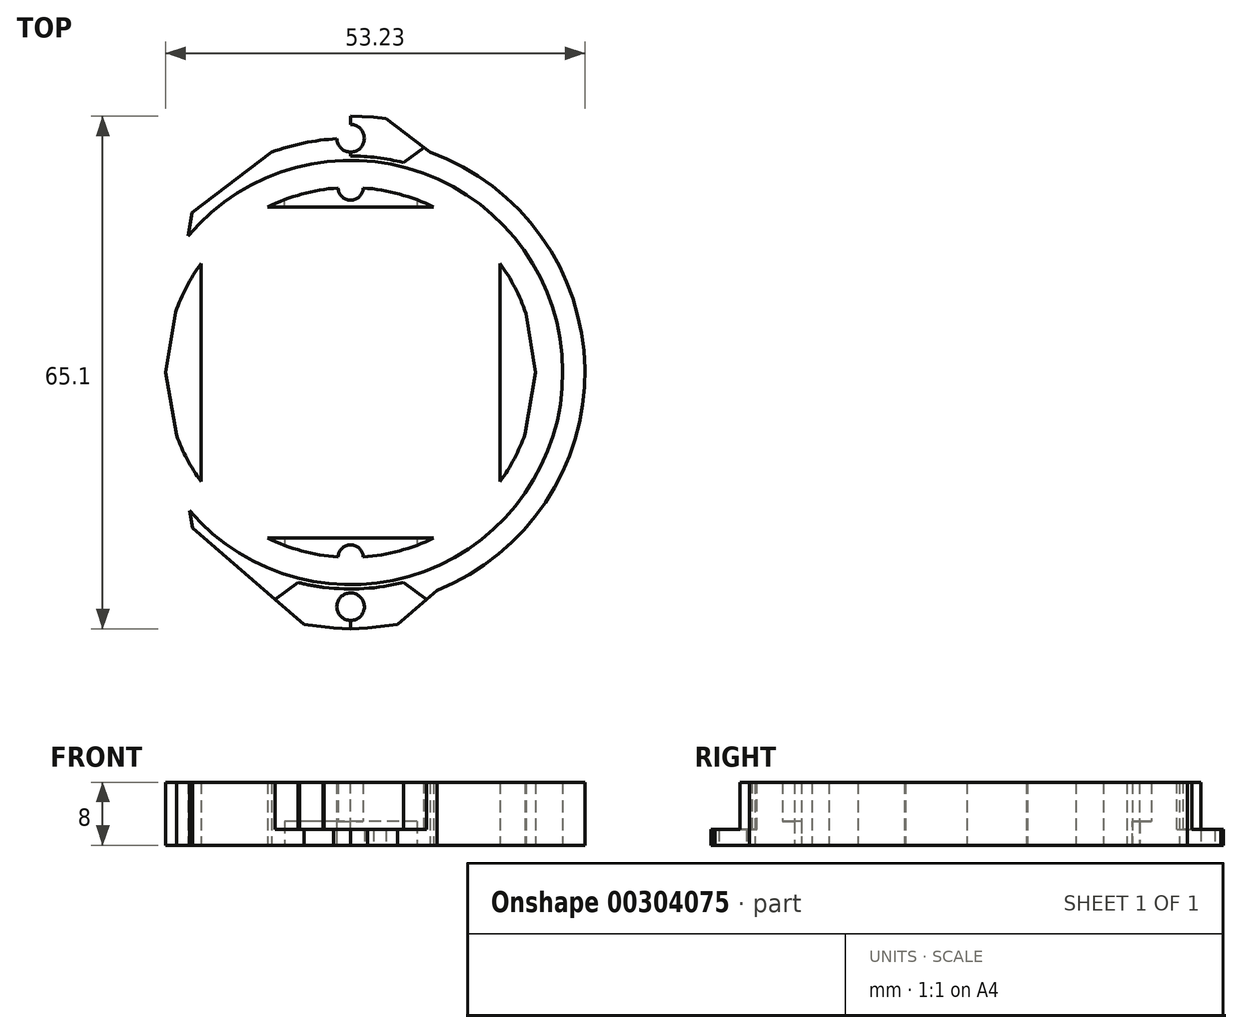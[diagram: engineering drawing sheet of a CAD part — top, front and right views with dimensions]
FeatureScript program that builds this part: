
annotation { "Feature Type Name" : "Feature", "Feature Type Description" : "" }
export const myFeature = defineFeature(function(context is Context, id is Id, definition is map)
    precondition{}
    {
        {
            var Q0;
            Q0=qCreatedBy(makeId("Top.planeOp"),FACE);
            var sketch = newSketch(context, id + "F0", { "sketchPlane" : qUnion([Q0])});
            skCircle(sketch, "E0", {"center": v(0, 0) * mm, "radius": 29.75 * mm});
            skCircle(sketch, "E1.0", {"center": v(0, 0) * mm, "radius": 32.55 * mm});
            skCircle(sketch, "E2.0", {"center": v(0, 0) * mm, "radius": 26.95 * mm});
            skCircle(sketch, "E3", {"center": v(0, 29.75) * mm, "radius": 1.75 * mm});
            skCircle(sketch, "E4", {"center": v(0, -29.75) * mm, "radius": 1.75 * mm});
            skPoint(sketch, "E5.visualSharp", {"position": v(18.58, -23.24) * mm});
            skCircle(sketch, "E6", {"center": v(0, 0) * mm, "radius": 23.5 * mm});
            skCircle(sketch, "E7", {"center": v(0, -23.5) * mm, "radius": 1.6 * mm});
            skCircle(sketch, "E8", {"center": v(0, 23.5) * mm, "radius": 1.6 * mm});
            skLineSegment(sketch, "E9", {"start": v(0, -32.55) * mm, "end": v(2.18, -32.48) * mm});
            skLineSegment(sketch, "E10", {"start": v(2.18, -32.48) * mm, "end": v(5.95, -32) * mm});
            skLineSegment(sketch, "E11", {"start": v(5.95, -32) * mm, "end": v(20.12, -19.72) * mm});
            skLineSegment(sketch, "E12", {"start": v(20.12, -19.72) * mm, "end": v(23.5, 0) * mm});
            skLineSegment(sketch, "E13", {"start": v(23.5, 0) * mm, "end": v(20.16, 20.34) * mm});
            skLineSegment(sketch, "E14", {"start": v(20.16, 20.34) * mm, "end": v(4.5, 32.24) * mm});
            skLineSegment(sketch, "E15", {"start": v(4.5, 32.24) * mm, "end": v(2.88, 32.42) * mm});
            skLineSegment(sketch, "E16", {"start": v(2.88, 32.42) * mm, "end": v(0.01, 32.55) * mm});
            skLineSegment(sketch, "E17", {"start": v(0.01, 32.55) * mm, "end": v(0.01, 18.5) * mm});
            skLineSegment(sketch, "E18", {"start": v(0, -18.5) * mm, "end": v(0, -32.55) * mm});
            skLineSegment(sketch, "E19.MirrorCS", {"start": v(-2.86, 32.42) * mm, "end": v(0.01, 32.55) * mm});
            skLineSegment(sketch, "E20.MirrorCS", {"start": v(-4.47, 32.24) * mm, "end": v(-2.86, 32.42) * mm});
            skLineSegment(sketch, "E21.MirrorCS", {"start": v(-20.13, 20.34) * mm, "end": v(-4.47, 32.24) * mm});
            skLineSegment(sketch, "E22.MirrorCS", {"start": v(-23.48, 0) * mm, "end": v(-20.13, 20.34) * mm});
            skLineSegment(sketch, "E23.MirrorCS", {"start": v(-20.1, -19.72) * mm, "end": v(-23.48, 0) * mm});
            skLineSegment(sketch, "E24.MirrorCS", {"start": v(-5.92, -32) * mm, "end": v(-20.1, -19.72) * mm});
            skLineSegment(sketch, "E25.MirrorCS", {"start": v(-2.16, -32.48) * mm, "end": v(-5.92, -32) * mm});
            skLineSegment(sketch, "E26.MirrorCS", {"start": v(0.02, -32.55) * mm, "end": v(-2.16, -32.48) * mm});
            skLineSegment(sketch, "E27.MirrorCS", {"start": v(0.02, -18.5) * mm, "end": v(0.02, -32.55) * mm});
            skSolve(sketch);
        }
        {
            var Q0;
            {var subQ0=sQuery(id+"F0.wireOp",EDGE,"E19.MirrorCS");Q0=makeQuery(id+"F0.imprint","IMPRINT",FACE,{"disambiguationData":[TD([[makeQuery(id+"F0.imprint","IMPRINT",EDGE,{"derivedFrom":subQ0}),-1.0]])]});}
            var Q1;
            {var subQ0=sQuery(id+"F0.wireOp",EDGE,"E15");Q1=makeQuery(id+"F0.imprint","IMPRINT",FACE,{"disambiguationData":[TD([[makeQuery(id+"F0.imprint","IMPRINT",EDGE,{"derivedFrom":subQ0}),1.0]])]});}
            var Q2;
            {var subQ5=sQuery(id+"F0.wireOp",EDGE,"E3");var subQ6=sQuery(id+"F0.wireOp",EDGE,"E0");var subQ7=makeQuery(id+"F0.imprint","INTERSECT",VERTEX,{"disambiguationData":[OD(0.0)],"derivedFrom":[subQ6,subQ5]});Q2=makeQuery(id+"F0.imprint","IMPRINT",FACE,{"disambiguationData":[TD([[makeQuery(id+"F0.imprint","IMPRINT",EDGE,{"disambiguationData":[TD([[subQ7,1.0]])],"derivedFrom":subQ6}),1.0]])]});}
            var Q3;
            {var subQ1=sQuery(id+"F0.wireOp",EDGE,"E3");var subQ9=sQuery(id+"F0.wireOp",EDGE,"E0");var subQ10=makeQuery(id+"F0.imprint","INTERSECT",VERTEX,{"disambiguationData":[OD(1.0)],"derivedFrom":[subQ9,subQ1]});Q3=makeQuery(id+"F0.imprint","IMPRINT",FACE,{"disambiguationData":[TD([[makeQuery(id+"F0.imprint","IMPRINT",EDGE,{"disambiguationData":[TD([[subQ10,-1.0]])],"derivedFrom":subQ9}),1.0]])]});}
            var Q4;
            {var subQ0=sQuery(id+"F0.wireOp",EDGE,"E17");var subQ1=sQuery(id+"F0.wireOp",EDGE,"E2.0");var subQ2=makeQuery(id+"F0.imprint","INTERSECT",VERTEX,{"derivedFrom":[subQ1,subQ0]});Q4=makeQuery(id+"F0.imprint","IMPRINT",FACE,{"disambiguationData":[TD([[makeQuery(id+"F0.imprint","IMPRINT",EDGE,{"disambiguationData":[TD([[subQ2,1.0]])],"derivedFrom":subQ1}),-1.0]])]});}
            var Q5;
            {var subQ1=sQuery(id+"F0.wireOp",EDGE,"E2.0");var subQ7=sQuery(id+"F0.wireOp",EDGE,"E17");var subQ9=makeQuery(id+"F0.imprint","INTERSECT",VERTEX,{"derivedFrom":[subQ1,subQ7]});Q5=makeQuery(id+"F0.imprint","IMPRINT",FACE,{"disambiguationData":[TD([[makeQuery(id+"F0.imprint","IMPRINT",EDGE,{"disambiguationData":[TD([[subQ9,-1.0]])],"derivedFrom":subQ1}),-1.0]])]});}
            var Q6;
            {var subQ2=sQuery(id+"F0.wireOp",EDGE,"E6");var subQ4=sQuery(id+"F0.wireOp",EDGE,"E13");var subQ14=makeQuery(id+"F0.imprint","INTERSECT",VERTEX,{"derivedFrom":[subQ2,subQ4]});Q6=makeQuery(id+"F0.imprint","IMPRINT",FACE,{"disambiguationData":[TD([[makeQuery(id+"F0.imprint","IMPRINT",EDGE,{"disambiguationData":[TD([[subQ14,-1.0]])],"derivedFrom":subQ2}),1.0]])]});}
            var Q7;
            {var subQ0=sQuery(id+"F0.wireOp",EDGE,"E18");var subQ1=sQuery(id+"F0.wireOp",EDGE,"E2.0");var subQ2=makeQuery(id+"F0.imprint","INTERSECT",VERTEX,{"derivedFrom":[subQ1,subQ0]});Q7=makeQuery(id+"F0.imprint","IMPRINT",FACE,{"disambiguationData":[TD([[makeQuery(id+"F0.imprint","IMPRINT",EDGE,{"disambiguationData":[TD([[subQ2,-1.0]])],"derivedFrom":subQ1}),-1.0]])]});}
            var Q8;
            {var subQ7=sQuery(id+"F0.wireOp",EDGE,"E24.MirrorCS");var subQ9=sQuery(id+"F0.wireOp",EDGE,"E0");var subQ10=makeQuery(id+"F0.imprint","INTERSECT",VERTEX,{"derivedFrom":[subQ9,subQ7]});Q8=makeQuery(id+"F0.imprint","IMPRINT",FACE,{"disambiguationData":[TD([[makeQuery(id+"F0.imprint","IMPRINT",EDGE,{"disambiguationData":[TD([[subQ10,-1.0]])],"derivedFrom":subQ9}),1.0]])]});}
            var Q9;
            {var subQ0=sQuery(id+"F0.wireOp",EDGE,"E25.MirrorCS");Q9=makeQuery(id+"F0.imprint","IMPRINT",FACE,{"disambiguationData":[TD([[makeQuery(id+"F0.imprint","IMPRINT",EDGE,{"derivedFrom":subQ0}),-1.0]])]});}
            var Q10;
            {var subQ0=sQuery(id+"F0.wireOp",EDGE,"E10");Q10=makeQuery(id+"F0.imprint","IMPRINT",FACE,{"disambiguationData":[TD([[makeQuery(id+"F0.imprint","IMPRINT",EDGE,{"derivedFrom":subQ0}),1.0]])]});}
            var Q11;
            {var subQ7=sQuery(id+"F0.wireOp",EDGE,"E0");var subQ9=sQuery(id+"F0.wireOp",EDGE,"E4");var subQ10=makeQuery(id+"F0.imprint","INTERSECT",VERTEX,{"disambiguationData":[OD(1.0)],"derivedFrom":[subQ7,subQ9]});Q11=makeQuery(id+"F0.imprint","IMPRINT",FACE,{"disambiguationData":[TD([[makeQuery(id+"F0.imprint","IMPRINT",EDGE,{"disambiguationData":[TD([[subQ10,-1.0]])],"derivedFrom":subQ7}),1.0]])]});}
            var Q12;
            {var subQ0=sQuery(id+"F0.wireOp",EDGE,"E12");var subQ1=sQuery(id+"F0.wireOp",EDGE,"E2.0");var subQ2=makeQuery(id+"F0.imprint","INTERSECT",VERTEX,{"derivedFrom":[subQ1,subQ0]});Q12=makeQuery(id+"F0.imprint","IMPRINT",FACE,{"disambiguationData":[TD([[makeQuery(id+"F0.imprint","IMPRINT",EDGE,{"disambiguationData":[TD([[subQ2,-1.0]])],"derivedFrom":subQ1}),-1.0]])]});}
            extrude(context, id + "F1", {"entities" : qUnion([Q0, Q1, Q2, Q3, Q4, Q5, Q6, Q7, Q8, Q9, Q10, Q11, Q12]), "depth" : 8 * mm});
        }
        {
            var Q0;
            Q0=makeQuery(id+"F1.opExtrude","CAP_FACE",FACE,{"disambiguationData":[OSD([sQuery(id+"F0.wireOp",EDGE,"E3"),sQuery(id+"F0.wireOp",EDGE,"E4"),sQuery(id+"F0.wireOp",EDGE,"E7"),sQuery(id+"F0.wireOp",EDGE,"E8"),sQuery(id+"F0.wireOp",EDGE,"5pVUo4Kb-ogc3-tZgz-UWGt-Z78I515m52U4.bottom"),sQuery(id+"F0.wireOp",EDGE,"5pVUo4Kb-ogc3-tZgz-UWGt-Z78I515m52U4.top"),sQuery(id+"F0.wireOp",EDGE,"5pVUo4Kb-ogc3-tZgz-UWGt-Z78I515m52U4.left"),sQuery(id+"F0.wireOp",EDGE,"5pVUo4Kb-ogc3-tZgz-UWGt-Z78I515m52U4.right"),sQuery(id+"F0.wireOp",EDGE,"E9"),sQuery(id+"F0.wireOp",EDGE,"E10"),sQuery(id+"F0.wireOp",EDGE,"E11"),sQuery(id+"F0.wireOp",EDGE,"E12"),sQuery(id+"F0.wireOp",EDGE,"E13"),sQuery(id+"F0.wireOp",EDGE,"E14"),sQuery(id+"F0.wireOp",EDGE,"E15"),sQuery(id+"F0.wireOp",EDGE,"E16"),sQuery(id+"F0.wireOp",EDGE,"2KKQg4aQ-yS0h-yKgR-9ZTe-73FSqlJjfBOo"),sQuery(id+"F0.wireOp",EDGE,"E18"),sQuery(id+"F0.wireOp",EDGE,"E19.MirrorCS"),sQuery(id+"F0.wireOp",EDGE,"E20.MirrorCS"),sQuery(id+"F0.wireOp",EDGE,"E21.MirrorCS"),sQuery(id+"F0.wireOp",EDGE,"E22.MirrorCS"),sQuery(id+"F0.wireOp",EDGE,"E23.MirrorCS"),sQuery(id+"F0.wireOp",EDGE,"E24.MirrorCS"),sQuery(id+"F0.wireOp",EDGE,"E25.MirrorCS"),sQuery(id+"F0.wireOp",EDGE,"E26.MirrorCS"),sQuery(id+"F0.wireOp",EDGE,"E27.MirrorCS"),sQuery(id+"F0.wireOp",EDGE,"c75564e2-3189-4455-9674-b0ccb1b02a3b0.MirrorCS"),sQuery(id+"F0.wireOp",EDGE,"ed3be647-e90e-411c-974e-45ce07631a0a0.MirrorCS")])],"isStart":false});
            var sketch = newSketch(context, id + "F2", { "sketchPlane" : qUnion([Q0])});
            skCircle(sketch, "E28", {"center": v(0, 0) * mm, "radius": 27.5 * mm});
            skLineSegment(sketch, "E29", {"start": v(0.01, 27.5) * mm, "end": v(3.45, 27.28) * mm});
            skLineSegment(sketch, "E30", {"start": v(3.45, 27.28) * mm, "end": v(6.7, 26.67) * mm});
            skLineSegment(sketch, "E31", {"start": v(6.7, 26.67) * mm, "end": v(13.63, 31.72) * mm});
            skLineSegment(sketch, "E32", {"start": v(13.63, 31.72) * mm, "end": v(0.02, 37.18) * mm});
            skLineSegment(sketch, "E33", {"start": v(0.02, 37.18) * mm, "end": v(0.01, 27.5) * mm});
            skLineSegment(sketch, "E34.MirrorCS", {"start": v(-13.6, 31.75) * mm, "end": v(0.02, 37.18) * mm});
            skLineSegment(sketch, "E35.MirrorCS", {"start": v(-6.69, 26.69) * mm, "end": v(-13.6, 31.75) * mm});
            skLineSegment(sketch, "E36.MirrorCS", {"start": v(-3.43, 27.3) * mm, "end": v(-6.69, 26.69) * mm});
            skLineSegment(sketch, "E37.MirrorCS", {"start": v(0.01, 27.5) * mm, "end": v(-3.43, 27.3) * mm});
            skLineSegment(sketch, "E38.MirrorCS", {"start": v(-13.6, -31.75) * mm, "end": v(0.02, -37.18) * mm});
            skLineSegment(sketch, "E39.MirrorCS", {"start": v(-6.69, -26.69) * mm, "end": v(-13.6, -31.75) * mm});
            skLineSegment(sketch, "E40.MirrorCS", {"start": v(-3.43, -27.3) * mm, "end": v(-6.69, -26.69) * mm});
            skLineSegment(sketch, "E41.MirrorCS", {"start": v(0.01, -27.5) * mm, "end": v(-3.43, -27.3) * mm});
            skLineSegment(sketch, "E42.MirrorCS", {"start": v(0.01, -27.5) * mm, "end": v(3.45, -27.28) * mm});
            skLineSegment(sketch, "E43.MirrorCS", {"start": v(3.45, -27.28) * mm, "end": v(6.7, -26.67) * mm});
            skLineSegment(sketch, "E44.MirrorCS", {"start": v(6.7, -26.67) * mm, "end": v(13.63, -31.72) * mm});
            skLineSegment(sketch, "E45.MirrorCS", {"start": v(13.63, -31.72) * mm, "end": v(0.02, -37.18) * mm});
            skSolve(sketch);
        }
        {
            var Q0;
            {var subQ2=sQuery(id+"F2.wireOp",EDGE,"E34.MirrorCS");Q0=makeQuery(id+"F2.imprint","IMPRINT",FACE,{"disambiguationData":[TD([[makeQuery(id+"F2.imprint","IMPRINT",EDGE,{"derivedFrom":subQ2}),-1.0]])]});}
            var Q1;
            {var subQ11=makeQuery(id+"F1.opExtrude","CAP_EDGE",EDGE,{"disambiguationData":[OSD([sQuery(id+"F0.wireOp",EDGE,"E15")])],"isStart":false});Q1=makeQuery(id+"F2.imprint","IMPRINT",FACE,{"disambiguationData":[TD([[makeQuery(id+"F2.imprint","IMPRINT",EDGE,{"derivedFrom":subQ11}),1.0]])]});}
            var Q2;
            {var subQ6=makeQuery(id+"F1.opExtrude","CAP_EDGE",EDGE,{"disambiguationData":[OSD([sQuery(id+"F0.wireOp",EDGE,"E19.MirrorCS")])],"isStart":false});Q2=makeQuery(id+"F2.imprint","IMPRINT",FACE,{"disambiguationData":[TD([[makeQuery(id+"F2.imprint","IMPRINT",EDGE,{"derivedFrom":subQ6}),-1.0]])]});}
            var Q3;
            {var subQ15=sQuery(id+"F2.wireOp",EDGE,"E38.MirrorCS");Q3=makeQuery(id+"F2.imprint","IMPRINT",FACE,{"disambiguationData":[TD([[makeQuery(id+"F2.imprint","IMPRINT",EDGE,{"derivedFrom":subQ15}),1.0]])]});}
            var Q4;
            {var subQ1=makeQuery(id+"F1.opExtrude","CAP_EDGE",EDGE,{"disambiguationData":[OSD([sQuery(id+"F0.wireOp",EDGE,"E25.MirrorCS")])],"isStart":false});Q4=makeQuery(id+"F2.imprint","IMPRINT",FACE,{"disambiguationData":[TD([[makeQuery(id+"F2.imprint","IMPRINT",EDGE,{"derivedFrom":subQ1}),-1.0]])]});}
            var Q5;
            {var subQ17=sQuery(id+"F0.wireOp",EDGE,"E9");Q5=makeQuery(id+"F2.imprint","IMPRINT",FACE,{"disambiguationData":[TD([[makeQuery(id+"F2.imprint","IMPRINT",EDGE,{"derivedFrom":makeQuery(id+"F1.opExtrude","CAP_EDGE",EDGE,{"disambiguationData":[OSD([subQ17])],"isStart":false})}),1.0]])]});}
            extrude(context, id + "F3", {"entities" : qUnion([Q0, Q1, Q2, Q3, Q4, Q5]), "operationType" : NewBodyOperationType.REMOVE, "oppositeDirection" : true, "depth" : 6 * mm});
        }
        {
            var Q0;
            Q0=makeQuery(id+"F1.opExtrude","CAP_FACE",FACE,{"disambiguationData":[OSD([sQuery(id+"F0.wireOp",EDGE,"E3"),sQuery(id+"F0.wireOp",EDGE,"E4"),sQuery(id+"F0.wireOp",EDGE,"E7"),sQuery(id+"F0.wireOp",EDGE,"E8"),sQuery(id+"F0.wireOp",EDGE,"5pVUo4Kb-ogc3-tZgz-UWGt-Z78I515m52U4.bottom"),sQuery(id+"F0.wireOp",EDGE,"5pVUo4Kb-ogc3-tZgz-UWGt-Z78I515m52U4.top"),sQuery(id+"F0.wireOp",EDGE,"5pVUo4Kb-ogc3-tZgz-UWGt-Z78I515m52U4.left"),sQuery(id+"F0.wireOp",EDGE,"5pVUo4Kb-ogc3-tZgz-UWGt-Z78I515m52U4.right"),sQuery(id+"F0.wireOp",EDGE,"E9"),sQuery(id+"F0.wireOp",EDGE,"E10"),sQuery(id+"F0.wireOp",EDGE,"E11"),sQuery(id+"F0.wireOp",EDGE,"E12"),sQuery(id+"F0.wireOp",EDGE,"E13"),sQuery(id+"F0.wireOp",EDGE,"E14"),sQuery(id+"F0.wireOp",EDGE,"E15"),sQuery(id+"F0.wireOp",EDGE,"E16"),sQuery(id+"F0.wireOp",EDGE,"2KKQg4aQ-yS0h-yKgR-9ZTe-73FSqlJjfBOo"),sQuery(id+"F0.wireOp",EDGE,"E18"),sQuery(id+"F0.wireOp",EDGE,"E19.MirrorCS"),sQuery(id+"F0.wireOp",EDGE,"E20.MirrorCS"),sQuery(id+"F0.wireOp",EDGE,"E21.MirrorCS"),sQuery(id+"F0.wireOp",EDGE,"E22.MirrorCS"),sQuery(id+"F0.wireOp",EDGE,"E23.MirrorCS"),sQuery(id+"F0.wireOp",EDGE,"E24.MirrorCS"),sQuery(id+"F0.wireOp",EDGE,"E25.MirrorCS"),sQuery(id+"F0.wireOp",EDGE,"E26.MirrorCS"),sQuery(id+"F0.wireOp",EDGE,"E27.MirrorCS"),sQuery(id+"F0.wireOp",EDGE,"c75564e2-3189-4455-9674-b0ccb1b02a3b0.MirrorCS"),sQuery(id+"F0.wireOp",EDGE,"ed3be647-e90e-411c-974e-45ce07631a0a0.MirrorCS")])],"isStart":true});
            var sketch = newSketch(context, id + "F4", { "sketchPlane" : qUnion([Q0])});
            skCircle(sketch, "E46", {"center": v(0, 0) * mm, "radius": 82.62 * mm});
            skLineSegment(sketch, "E47.bottom", {"start": v(22.33, -27.5) * mm, "end": v(-22.33, -27.5) * mm});
            skLineSegment(sketch, "E47.top", {"start": v(22.33, 27.5) * mm, "end": v(-22.33, 27.5) * mm});
            skLineSegment(sketch, "E47.left", {"start": v(22.33, -27.5) * mm, "end": v(22.33, 27.5) * mm});
            skLineSegment(sketch, "E47.right", {"start": v(-22.33, -27.5) * mm, "end": v(-22.33, 27.5) * mm});
            skLineSegment(sketch, "E48.bottom", {"start": v(8.46, 20.73) * mm, "end": v(-8.41, 20.73) * mm});
            skLineSegment(sketch, "E48.top", {"start": v(8.46, 29.47) * mm, "end": v(-8.41, 29.47) * mm});
            skLineSegment(sketch, "E48.left", {"start": v(8.46, 20.73) * mm, "end": v(8.46, 29.47) * mm});
            skLineSegment(sketch, "E48.right", {"start": v(-8.41, 20.73) * mm, "end": v(-8.41, 29.47) * mm});
            skPoint(sketch, "E48.middle", {"position": v(0.02, 25.1) * mm});
            skLineSegment(sketch, "E49", {"start": v(0.02, 27.5) * mm, "end": v(8.46, 27.5) * mm});
            skLineSegment(sketch, "E50", {"start": v(8.46, 27.5) * mm, "end": v(8.46, 20.73) * mm});
            skLineSegment(sketch, "E51", {"start": v(-8.41, 20.73) * mm, "end": v(-8.41, 27.5) * mm});
            skLineSegment(sketch, "E52", {"start": v(-8.41, 27.5) * mm, "end": v(8.46, 27.5) * mm});
            skLineSegment(sketch, "E53.MirrorCS", {"start": v(8.46, -20.73) * mm, "end": v(-8.41, -20.73) * mm});
            skLineSegment(sketch, "E54.MirrorCS", {"start": v(8.46, -27.5) * mm, "end": v(8.46, -20.73) * mm});
            skLineSegment(sketch, "E55.MirrorCS", {"start": v(-8.41, -27.5) * mm, "end": v(8.46, -27.5) * mm});
            skLineSegment(sketch, "E56.MirrorCS", {"start": v(-8.41, -20.73) * mm, "end": v(-8.41, -27.5) * mm});
            skSolve(sketch);
        }
        {
            var Q0;
            Q0=makeQuery(id+"F4.imprint","IMPRINT",FACE,{"disambiguationData":[TD([[makeQuery(id+"F4.imprint","IMPRINT",EDGE,{"derivedFrom":sQuery(id+"F4.wireOp",EDGE,"E48.bottom")}),-1.0]])]});
            var Q1;
            Q1=makeQuery(id+"F4.imprint","IMPRINT",FACE,{"disambiguationData":[TD([[makeQuery(id+"F4.imprint","IMPRINT",EDGE,{"derivedFrom":sQuery(id+"F4.wireOp",EDGE,"E53.MirrorCS")}),1.0]])]});
            extrude(context, id + "F5", {"entities" : qUnion([Q0, Q1]), "operationType" : NewBodyOperationType.REMOVE, "oppositeDirection" : true, "depth" : 3 * mm});
        }
        {
            var Q0;
            Q0=makeQuery(id+"F1.opExtrude","CAP_FACE",FACE,{"disambiguationData":[OSD([sQuery(id+"F0.wireOp",EDGE,"E3"),sQuery(id+"F0.wireOp",EDGE,"E4"),sQuery(id+"F0.wireOp",EDGE,"E7"),sQuery(id+"F0.wireOp",EDGE,"E8"),sQuery(id+"F0.wireOp",EDGE,"E9"),sQuery(id+"F0.wireOp",EDGE,"E10"),sQuery(id+"F0.wireOp",EDGE,"E11"),sQuery(id+"F0.wireOp",EDGE,"E12"),sQuery(id+"F0.wireOp",EDGE,"E13"),sQuery(id+"F0.wireOp",EDGE,"E14"),sQuery(id+"F0.wireOp",EDGE,"E15"),sQuery(id+"F0.wireOp",EDGE,"E16"),sQuery(id+"F0.wireOp",EDGE,"E18"),sQuery(id+"F0.wireOp",EDGE,"E19.MirrorCS"),sQuery(id+"F0.wireOp",EDGE,"E20.MirrorCS"),sQuery(id+"F0.wireOp",EDGE,"E21.MirrorCS"),sQuery(id+"F0.wireOp",EDGE,"E22.MirrorCS"),sQuery(id+"F0.wireOp",EDGE,"E23.MirrorCS"),sQuery(id+"F0.wireOp",EDGE,"E24.MirrorCS"),sQuery(id+"F0.wireOp",EDGE,"E25.MirrorCS"),sQuery(id+"F0.wireOp",EDGE,"E26.MirrorCS"),sQuery(id+"F0.wireOp",EDGE,"E27.MirrorCS")])],"isStart":true});
            var sketch = newSketch(context, id + "F6", { "sketchPlane" : qUnion([Q0])});
            skLineSegment(sketch, "E57.bottom", {"start": v(16, 21) * mm, "end": v(-16, 21) * mm});
            skLineSegment(sketch, "E57.top", {"start": v(16, -21) * mm, "end": v(-16, -21) * mm});
            skLineSegment(sketch, "E57.left", {"start": v(19, 18) * mm, "end": v(19, -18) * mm});
            skLineSegment(sketch, "E57.right", {"start": v(-19, 18) * mm, "end": v(-19, -18) * mm});
            skPoint(sketch, "E57.middle", {"position": v(0, 0) * mm});
            skPoint(sketch, "E58.visualSharp", {"position": v(-19, -21) * mm});
            skArc(sketch, "E58.filletArc", {"start": v(-19, -18) * mm, "mid": v(-18.12, -20.12) * mm, "end": v(-16, -21) * mm});
            skPoint(sketch, "E59.visualSharp", {"position": v(-19, 21) * mm});
            skArc(sketch, "E59.filletArc", {"start": v(-16, 21) * mm, "mid": v(-18.12, 20.12) * mm, "end": v(-19, 18) * mm});
            skPoint(sketch, "E60.visualSharp", {"position": v(19, 21) * mm});
            skArc(sketch, "E60.filletArc", {"start": v(19, 18) * mm, "mid": v(18.12, 20.12) * mm, "end": v(16, 21) * mm});
            skPoint(sketch, "E61.visualSharp", {"position": v(19, -21) * mm});
            skArc(sketch, "E61.filletArc", {"start": v(16, -21) * mm, "mid": v(18.12, -20.12) * mm, "end": v(19, -18) * mm});
            skSolve(sketch);
        }
        {
            var Q0;
            Q0=makeQuery(id+"F6.imprint","IMPRINT",FACE,{"disambiguationData":[TD([[makeQuery(id+"F6.imprint","IMPRINT",EDGE,{"derivedFrom":sQuery(id+"F6.wireOp",EDGE,"E57.left")}),-1.0]])]});
            var Q1;
            {var subQ5=makeQuery(id+"F5.boolean.opBoolean","COPY",EDGE,{"derivedFrom":makeQuery(id+"F5.opExtrude","CAP_EDGE",EDGE,{"disambiguationData":[OSD([sQuery(id+"F4.wireOp",EDGE,"E53.MirrorCS")])],"isStart":true})});Q1=makeQuery(id+"F6.imprint","IMPRINT",FACE,{"disambiguationData":[TD([[makeQuery(id+"F6.imprint","IMPRINT",EDGE,{"derivedFrom":subQ5}),1.0]])]});}
            var Q2;
            {var subQ5=makeQuery(id+"F5.boolean.opBoolean","COPY",EDGE,{"derivedFrom":makeQuery(id+"F5.opExtrude","CAP_EDGE",EDGE,{"disambiguationData":[OSD([sQuery(id+"F4.wireOp",EDGE,"E48.bottom")])],"isStart":true})});Q2=makeQuery(id+"F6.imprint","IMPRINT",FACE,{"disambiguationData":[TD([[makeQuery(id+"F6.imprint","IMPRINT",EDGE,{"derivedFrom":subQ5}),-1.0]])]});}
            extrude(context, id + "F7", {"entities" : qUnion([Q0, Q1, Q2]), "operationType" : NewBodyOperationType.REMOVE, "endBound" : BoundingType.THROUGH_ALL, "oppositeDirection" : true, "depth" : 25 * mm});
        }
    });
